# Revit family: IS_Dea_T5099_BIM_DE
name_source: partatom
category: Plumbing Fixtures
revit_build: Autodesk Revit MEP 2016 (Build: 20161004_0715(x64)
units: mm (PartAtom-declared; Revit-internal decimal feet)

## family parameters
Cut with Voids When Loaded = No
Host = Face
OmniClass Number = 23.45.05.14.14.14
OmniClass Title = Clinic Sinks
Part Type = Normal
Room Calculation Point = No
Round Connector Dimension = Use Diameter
Shared = Yes

## types (4) — shared parameters
Accessories = www.idealstandard.de\ersatzteile
AreaUnits = millimeters
Assembly Code = C1030200
AssetType = Fixed
BIMobject category = Bidets
Brand = Ideal Standard
Brand url = http://www.idealstandard.co.uk
CodePerformance = DIN EN 14528 CL 15, DIN EN 35
ConnectionType = Plumbing
CurrencyUnit = €
Date of publishing = 4/3/2017
Default Elevation = 800 mm
DurationUnit = year
Edition number = 1
ExpectedLife = 25
Features = DEA floor standing bidet 365x550mm, 1 taphole
GrossWeight = 26,2 kg
IFC Classification = Sanitary Terminal
Installation instructions = http://www.idealstandard.de
InstallationDate = 1900-12-31T23:59:59
InstallationInstructions = www.idealstandard.de\produkte
LinearUnits = millimeters
Manufacturer name = Ideal Standard
ManufacturerURL = www.idealstandard.de
Material = Vitreous china
Material main = Ceramics
Nominal height = 400 mm  [stored 1.31234 ft]
Nominal width = 365 mm
NominalLength = 551 mm
Product Guid = 83c15229-1e4d-4cde-833b-c5a0c9f7b139
Product SKU = T5099
Product data url = https://bimobject.com
Product family = DEA
Product group = Bidet
Product url = http://www.idealstandard.de
ProductInformation = www.idealstandard.de
QR code = http://bimobject.com
Shape = Sculptured
Size = 550 x 365 x 400 mm
Space = Internal
Technical description = http://www.idealstandard.de
URL = www.idealstandard.de
Uniclass 2.0 Code = PR-35-06-11
Uniclass 2.0 Description = Bidets
Uniclass 2015 Name = Bidets
Uniclass2015Code = Pr_40_20_06_11
Uniclass2015Title = Bidets
Uniclass2015Version = Products v1.1
Version = 1
VolumeUnits = Litres
Weight Net (Kg) = 24.5
zero-valued in all types: CWFU, Cost, HWFU, NominalDepth, WFU

## per-type parameters (varying)
| type | BIMObjectName | BarCode | Color | Description | EAN code | Finish | Model | ModelNumber | ModelReference | Name |
| T509901 DEA floor standing bidet 365x550mm, 1 taphole | ISI_IdealStandard_Washbasins_DEA_T509901 | 8014140407317 | White | DEA BTW BID WHITE 1TH OF | https://8014140407317 | White | T509901 | T509901 | IS Standbidet DEA, 1Hl., 365x550x400mm, Weiß | ISI_IdealStandard_Washbasins_DEA_T509901 |
| T509983 DEA floor standing bidet 365x550mm, 1 taphole | ISI_IdealStandard_Washbasins_DEA_T509983 | 8014140409700 | Matt White | DEA BTW BID MTT WHT 1TH OF | https://8014140409700 | Matt White | T509983 | T509983 | IS Standbidet DEA, 1Hl., 365x550x400mm, Weiß seidenmatt | ISI_IdealStandard_Washbasins_DEA_T509983 |
| T5099MA DEA floor standing bidet 365x550mm, 1 taphole | ISI_IdealStandard_Washbasins_DEA_T509983 | 8014140410744 | WHITE IP | DEA BTW BID MTT WHT 1TH OF | https://8014140410744 | Matt White | T5099MA | T509983 | IS Standbidet DEA, 1Hl., 365x550x400mm, Weiß seidenmatt | ISI_IdealStandard_Washbasins_DEA_T509983 |
| T5099MI DEA floor standing bidet 365x550mm, 1 taphole | ISI_IdealStandard_Washbasins_DEA_T509983 | 8014140423928 | Matt White IP | DEA BTW BID MTT WHT 1TH OF | https://8014140423928 | Matt White | T5099MI | T509983 | IS Standbidet DEA, 1Hl., 365x550x400mm, Weiß seidenmatt | ISI_IdealStandard_Washbasins_DEA_T509983 |

note: [stored X ft] marks values corroborated as IEEE doubles in the binary element streams (Revit-internal decimal feet)

## geometry (parser evidence)
native form markers: Blend x4, Sweep x2
no freeform markers — native parametric forms only
